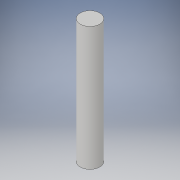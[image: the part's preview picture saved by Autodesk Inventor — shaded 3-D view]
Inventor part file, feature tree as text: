
AUTODESK INVENTOR PART (.ipt)
format: ipt  version: 2019 (Build 230136000, 136)  size: 90,112 bytes
history: native  units: mm
features: extrude x1, sketch x1
ambient origin geometry x8: Origin, YZ Plane, XZ Plane, XY Plane, X Axis, Y Axis, Z Axis, Center Point
bodies: Solid1 (feature_tree)
feature tree (2):
  extrude  "Extrusion1"  Depth=63.6mm TaperAngle=0.0deg
  sketch  "Sketch1"  dims[d0=10.0mm d1=63.6mm d2=0.0mm]
